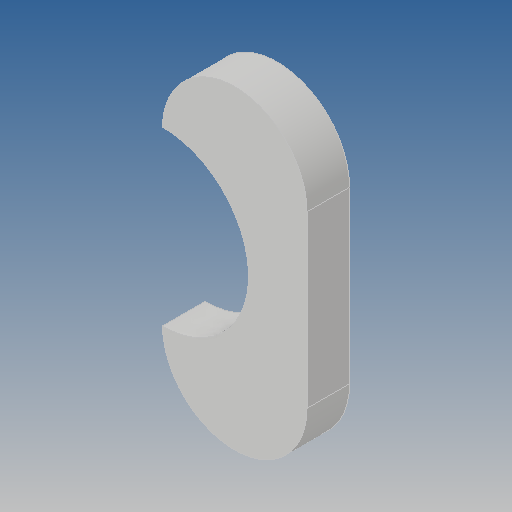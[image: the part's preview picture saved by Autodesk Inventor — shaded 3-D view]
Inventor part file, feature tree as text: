
AUTODESK INVENTOR PART (.ipt)
format: ipt  version: 2018 (Build 220112000, 112)  size: 103,936 bytes
history: native  units: mm
features: extrude x2, sketch x2, other x1
ambient origin geometry x8: Origin, YZ Plane, XZ Plane, XY Plane, X Axis, Y Axis, Z Axis, Center Point
bodies: Solid1 (feature_tree)
feature tree (5):
  other  "<userpath>\OneDrive\Objet3D\3DPrinter\Parameters.xlsx"
  extrude  "Extrusion1"  Depth=13.6mm
  extrude  "Extrusion2"  Depth=4.0mm
  sketch  "Sketch1"  dims[d0=16.0mm d1=13.6mm]
  sketch  "Sketch2"  dims[d3=4.0mm d4=0.0mm d5=16.2mm d6=0.0mm d7=0.0mm]
